# Revit family: L-office 32 Standart
name_source: partatom
category: Осветительные приборы
revit_build: Autodesk Revit 2017 (Build: 20160225_1515(x64)
units: mm (PartAtom-declared; Revit-internal decimal feet)

## family parameters
Всегда вертикально = Да
Заголовок OmniClass = Luminaries for Internal Lighting
Источник света = Да
Номер OmniClass = 23.80.70.11
Общий = Нет
Основа = Потолок
При загрузке вырезать с полостями = Нет
Размер круглого соединителя = Использовать диаметр
Тип детали = Нормальный
Точка расчета площади = Нет

## types (2) — shared parameters
Видимая форма излучения при визуализации = Да
Изготовитель = LEDEL
Излучение по длине прямоугольника = 590 мм
Излучение по ширине прямоугольника = 590 мм
Классификация нагрузок = Освещение
Комментарии к типоразмеру = Офисные
Кривая сил света = Д
Описание = Светильник L-office 32 Standart предназначен для установки в помещениях торгово-офисного и административного назначения.
Полная установленная мощность = 30 В·А
Расстояние от потолка до светильника = 150 мм
Световой поток светильника = 3900 лм
Светофильтр = 16777215
Смещение цветовой температуры при затухании лампы = <Нет>
Угол наклона = 90.00°

## per-type parameters (varying)
| type | Артикул | Файл фотометрической сетки | Цветовая температура |
| L-office 32 Standart 4.0K | 111203000842600 | L-office 32-30-Д-4.0K-02-Standart.ies | 4000 K |
| L-office 32 Standart 5.0K | 111203000852600 | L-office 32-30-Д-5.0K-02-Standart.ies | 5000 K |

## geometry (parser evidence)
native form markers: Sweep x2
no freeform markers — native parametric forms only
